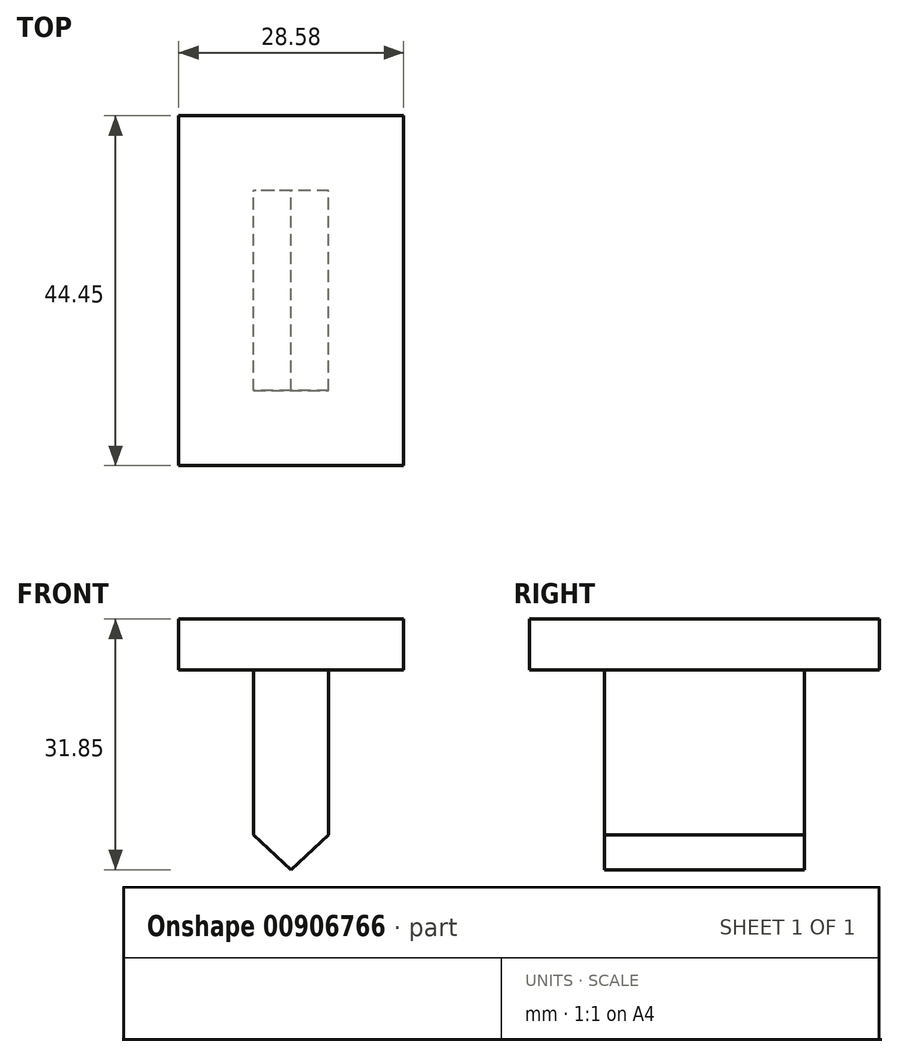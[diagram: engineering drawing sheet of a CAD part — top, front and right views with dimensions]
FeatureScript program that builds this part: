
annotation { "Feature Type Name" : "Feature", "Feature Type Description" : "" }
export const myFeature = defineFeature(function(context is Context, id is Id, definition is map)
    precondition{}
    {
        {
            var Q0;
            Q0=qCreatedBy(makeId("Front.planeOp"),FACE);
            var sketch = newSketch(context, id + "F0", { "sketchPlane" : qUnion([Q0])});
            skLineSegment(sketch, "E0", {"start": v(0, 0) * mm, "end": v(9.53, 0) * mm});
            skLineSegment(sketch, "E1", {"start": v(9.53, 0) * mm, "end": v(9.53, -20.95) * mm});
            skLineSegment(sketch, "E2", {"start": v(9.53, -20.95) * mm, "end": v(4.76, -25.4) * mm});
            skLineSegment(sketch, "E3", {"start": v(4.76, -25.4) * mm, "end": v(0, -20.95) * mm});
            skLineSegment(sketch, "E4", {"start": v(0, -20.95) * mm, "end": v(0, 0) * mm});
            skSolve(sketch);
        }
        {
            var Q0;
            Q0=makeQuery(id+"F0.imprint","IMPRINT",FACE,{"disambiguationData":[TD([[makeQuery(id+"F0.imprint","IMPRINT",EDGE,{"derivedFrom":sQuery(id+"F0.wireOp",EDGE,"E0")}),-1.0]])]});
            extrude(context, id + "F1", {"entities" : qUnion([Q0]), "depth" : 25.4 * mm, "offsetDistance" : 25.4 * mm});
        }
        {
            var Q0;
            Q0=makeQuery(id+"F1.opExtrude","CAP_FACE",FACE,{"disambiguationData":[OSD([sQuery(id+"F0.wireOp",EDGE,"E0"),sQuery(id+"F0.wireOp",EDGE,"E1"),sQuery(id+"F0.wireOp",EDGE,"E2"),sQuery(id+"F0.wireOp",EDGE,"E3"),sQuery(id+"F0.wireOp",EDGE,"E4")])],"isStart":true});
            var sketch = newSketch(context, id + "F2", { "sketchPlane" : qUnion([Q0])});
            skLineSegment(sketch, "E5", {"start": v(-19.05, 0) * mm, "end": v(-19.05, 6.45) * mm});
            skLineSegment(sketch, "E6", {"start": v(-19.05, 6.45) * mm, "end": v(9.52, 6.45) * mm});
            skLineSegment(sketch, "E7", {"start": v(-19.05, 0) * mm, "end": v(9.52, 0) * mm});
            skLineSegment(sketch, "E8", {"start": v(9.52, 0) * mm, "end": v(9.52, 6.45) * mm});
            skSolve(sketch);
        }
        {
            var Q0;
            {var subQ3=sQuery(id+"F2.wireOp",EDGE,"E5");Q0=makeQuery(id+"F2.imprint","IMPRINT",FACE,{"disambiguationData":[TD([[makeQuery(id+"F2.imprint","IMPRINT",EDGE,{"derivedFrom":subQ3}),-1.0]])]});}
            extrude(context, id + "F3", {"entities" : qUnion([Q0]), "operationType" : NewBodyOperationType.ADD, "oppositeDirection" : true, "depth" : 34.92 * mm, "offsetDistance" : 25.4 * mm});
        }
        {
            var Q0;
            Q0=makeQuery(id+"F3.boolean.opBoolean","MERGE",FACE,{"derivedFrom":[makeQuery(id+"F1.opExtrude","CAP_FACE",FACE,{"disambiguationData":[OSD([sQuery(id+"F0.wireOp",EDGE,"E0"),sQuery(id+"F0.wireOp",EDGE,"E1"),sQuery(id+"F0.wireOp",EDGE,"E2"),sQuery(id+"F0.wireOp",EDGE,"E3"),sQuery(id+"F0.wireOp",EDGE,"E4")])],"isStart":true}),makeQuery(id+"F3.opExtrude","CAP_FACE",FACE,{"disambiguationData":[OSD([sQuery(id+"F2.wireOp",EDGE,"E5"),sQuery(id+"F2.wireOp",EDGE,"E6"),sQuery(id+"F2.wireOp",EDGE,"E7"),sQuery(id+"F2.wireOp",EDGE,"E8")])],"isStart":true})]});
            var sketch = newSketch(context, id + "F4", { "sketchPlane" : qUnion([Q0])});
            skLineSegment(sketch, "E9", {"start": v(-19.05, 6.45) * mm, "end": v(-19.05, 0) * mm});
            skLineSegment(sketch, "E10", {"start": v(-19.05, 0) * mm, "end": v(9.52, 0) * mm});
            skLineSegment(sketch, "E11", {"start": v(9.52, 0) * mm, "end": v(9.52, 6.45) * mm});
            skLineSegment(sketch, "E12", {"start": v(9.52, 6.45) * mm, "end": v(-19.05, 6.45) * mm});
            skSolve(sketch);
        }
        {
            var Q0;
            Q0 = qSketchRegion(id + "F4", true);
            extrude(context, id + "F5", {"entities" : qUnion([Q0]), "operationType" : NewBodyOperationType.ADD, "depth" : 9.52 * mm, "offsetDistance" : 25.4 * mm});
        }
    });
